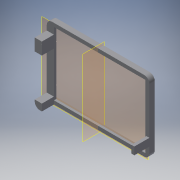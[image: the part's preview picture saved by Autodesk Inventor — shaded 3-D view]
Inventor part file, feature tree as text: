
AUTODESK INVENTOR PART (.ipt)
format: ipt  version: 2019.4 (Build 234330000, 330)  size: 274,432 bytes
history: native  units: mm
features: extrude x7, sketch x7, projected_geometry x6, reference x5, other x5, plane x2
ambient origin geometry x8: Origin, YZ Plane, XZ Plane, XY Plane, X Axis, Y Axis, Z Axis, Center Point
bodies: Solid1 (feature_tree)
feature tree (32):
  plane  "Work Plane1"
  extrude  "Extrusion1"  Depth=4.0mm
  extrude  "Extrusion2"  Depth=1.0mm
  extrude  "Extrusion3"  Depth=4.0mm TaperAngle=0.0deg
  plane  "Work Plane2"
  extrude  "Extrusion4"  Depth=2.0mm
  extrude  "Extrusion5"  Depth=2.0mm
  extrude  "Extrusion6"  Depth=4.0mm
  extrude  "Extrusion7"  Depth=16.0mm
  sketch  "Sketch1"  dims[d0=4.0mm d1=1.0mm]
  reference  "Reference1"
  reference  "Reference2"
  sketch  "Sketch2"  dims[d2=3.0mm d3=0.0mm d4=1.0mm]
  reference  "Reference3"
  projected_geometry  "Projected Loop1"
  sketch  "Sketch3"  dims[d5=0.5mm d6=4.0mm d7=0.0mm]
  projected_geometry  "Projected Loop2"
  sketch  "Sketch4"  dims[d8=20.0mm d9=0.0mm d10=2.0mm]
  projected_geometry  "Projected Loop3"
  reference  "Reference4"
  reference  "Reference5"
  sketch  "Sketch5"  dims[d11=2.0mm d12=2.0mm]
  projected_geometry  "Projected Loop4"
  sketch  "Sketch6"  dims[d13=2.0mm d14=4.0mm]
  projected_geometry  "Projected Loop5"
  projected_geometry  "Projected Loop6"
  sketch  "Sketch7"  dims[d15=10.0mm d20=16.0mm d21=16.0mm d22=0.0mm d23=14.0mm d24=2.8mm d25=2.8mm d26=16.0mm d27=0.0mm d28=13.5mm d29=9.0mm d30=9.0mm d31=3.0mm d32=16.0mm d33=0.0mm d34=16.0mm d35=0.0mm]
  other  "Full_HITscope_v0.iam"
  other  "00_24wellplate_base_2:1"
  other  "03_Omniscope_lid_lenses:1"
  other  "00_Microlinearmotor:2"
  other  "00_Microlinearmotor:1"
